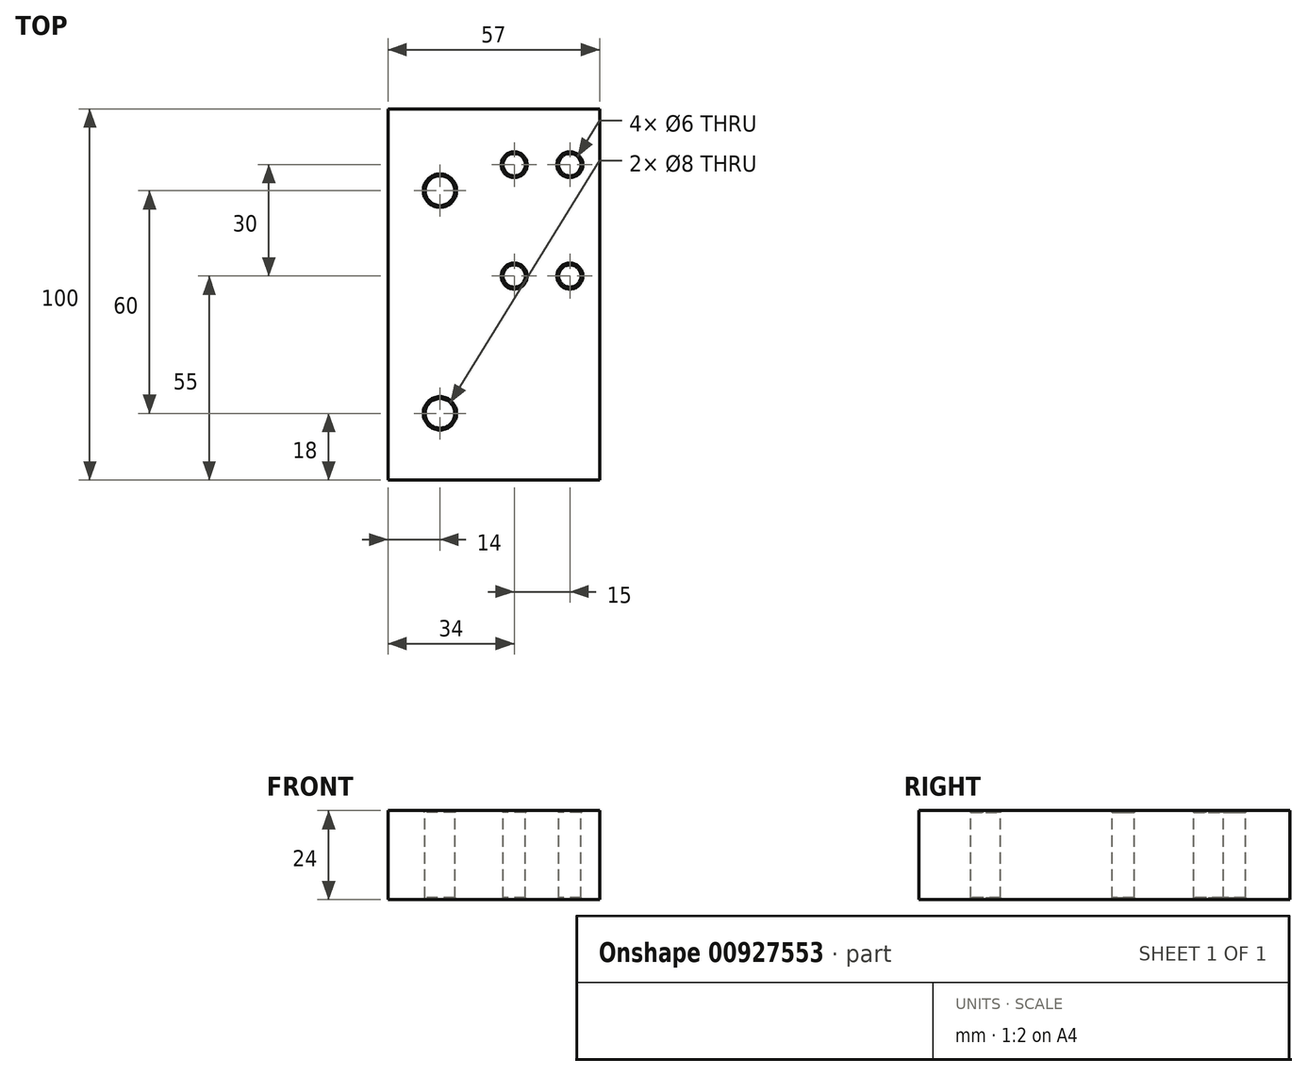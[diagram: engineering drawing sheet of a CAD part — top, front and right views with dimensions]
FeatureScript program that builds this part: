
annotation { "Feature Type Name" : "Feature", "Feature Type Description" : "" }
export const myFeature = defineFeature(function(context is Context, id is Id, definition is map)
    precondition{}
    {
        {
            var Q0;
            Q0=qCreatedBy(makeId("Right.planeOp"),FACE);
            var sketch = newSketch(context, id + "F0", { "sketchPlane" : qUnion([Q0])});
            skLineSegment(sketch, "E0.bottom", {"start": v(50, -12) * mm, "end": v(-50, -12) * mm});
            skLineSegment(sketch, "E0.top", {"start": v(50, 12) * mm, "end": v(-50, 12) * mm});
            skLineSegment(sketch, "E0.left", {"start": v(50, -12) * mm, "end": v(50, 12) * mm});
            skLineSegment(sketch, "E0.right", {"start": v(-50, -12) * mm, "end": v(-50, 12) * mm});
            skPoint(sketch, "E0.middle", {"position": v(0, 0) * mm});
            skSolve(sketch);
        }
        {
            var Q0;
            Q0 = qSketchRegion(id + "F0", true);
            extrude(context, id + "F1", {"entities" : qUnion([Q0]), "oppositeDirection" : true, "depth" : 22 * mm, "offsetDistance" : 25 * mm});
        }
        {
            var Q0;
            Q0=makeQuery(id+"F1.opExtrude","SWEPT_FACE",FACE,{"disambiguationData":[OSD([sQuery(id+"F0.wireOp",EDGE,"E0.top")])]});
            var sketch = newSketch(context, id + "F2", { "sketchPlane" : qUnion([Q0])});
            skLineSegment(sketch, "E1", {"start": v(-63.87, 28) * mm, "end": v(57.84, 28) * mm, "construction": true});
            skLineSegment(sketch, "E2", {"start": v(-8, 56.96) * mm, "end": v(-8, -60.17) * mm, "construction": true});
            skCircle(sketch, "E3", {"center": v(-8, 28) * mm, "radius": 4 * mm});
            skCircle(sketch, "E4", {"center": v(-8, -32) * mm, "radius": 4 * mm});
            skLineSegment(sketch, "E5", {"start": v(-58.28, -2) * mm, "end": v(56.2, -2) * mm, "construction": true});
            skSolve(sketch);
        }
        {
            var Q0;
            Q0 = qSketchRegion(id + "F2", true);
            extrude(context, id + "F3", {"entities" : qUnion([Q0]), "operationType" : NewBodyOperationType.REMOVE, "endBound" : BoundingType.THROUGH_ALL, "oppositeDirection" : true, "depth" : 25 * mm, "offsetDistance" : 25 * mm});
        }
        {
            var Q0;
            Q0=makeQuery(id+"F3.boolean.opBoolean","COPY",FACE,{"derivedFrom":makeQuery(id+"F3.opExtrude","SWEPT_FACE",FACE,{"disambiguationData":[OSD([sQuery(id+"F2.wireOp",EDGE,"E3")])]})});
            var Q1;
            Q1=makeQuery(id+"F3.boolean.opBoolean","COPY",FACE,{"derivedFrom":makeQuery(id+"F3.opExtrude","SWEPT_FACE",FACE,{"disambiguationData":[OSD([sQuery(id+"F2.wireOp",EDGE,"E4")])]})});
            chamfer(context, id + "F4", {"entities" : qUnion([Q0, Q1]), "width" : 0.5 * mm, "tangentPropagation" : true});
        }
        {
            var Q0;
            Q0=makeQuery(id+"F1.opExtrude","CAP_FACE",FACE,{"disambiguationData":[OSD([sQuery(id+"F0.wireOp",EDGE,"E0.bottom"),sQuery(id+"F0.wireOp",EDGE,"E0.top"),sQuery(id+"F0.wireOp",EDGE,"E0.left"),sQuery(id+"F0.wireOp",EDGE,"E0.right")])],"isStart":true});
            var sketch = newSketch(context, id + "F5", { "sketchPlane" : qUnion([Q0])});
            skLineSegment(sketch, "E6", {"start": v(35, 33.56) * mm, "end": v(35, -35.07) * mm, "construction": true});
            skLineSegment(sketch, "E7", {"start": v(5, 29.86) * mm, "end": v(5, -24.68) * mm, "construction": true});
            skLineSegment(sketch, "E8", {"start": v(50, 13.58) * mm, "end": v(50, -15.06) * mm, "construction": true});
            skLineSegment(sketch, "E9", {"start": v(-50, 13.27) * mm, "end": v(-50, -17.52) * mm, "construction": true});
            skLineSegment(sketch, "E10", {"start": v(-50, 12) * mm, "end": v(50, 12) * mm});
            skLineSegment(sketch, "E11", {"start": v(50, 12) * mm, "end": v(50, -12) * mm});
            skLineSegment(sketch, "E12", {"start": v(50, -12) * mm, "end": v(-50, -12) * mm});
            skLineSegment(sketch, "E13", {"start": v(-50, -12) * mm, "end": v(-50, 12) * mm});
            skSolve(sketch);
        }
        {
            var Q0;
            Q0 = qSketchRegion(id + "F5", true);
            extrude(context, id + "F6", {"entities" : qUnion([Q0]), "operationType" : NewBodyOperationType.ADD, "depth" : 35 * mm, "offsetDistance" : 25 * mm});
        }
        {
            var Q0;
            Q0=makeQuery(id+"F6.boolean.opBoolean","MERGE",FACE,{"derivedFrom":[makeQuery(id+"F1.opExtrude","SWEPT_FACE",FACE,{"disambiguationData":[OSD([sQuery(id+"F0.wireOp",EDGE,"E0.top")])]}),makeQuery(id+"F6.opExtrude","SWEPT_FACE",FACE,{"disambiguationData":[OSD([sQuery(id+"F5.wireOp",EDGE,"E10")])]})]});
            var sketch = newSketch(context, id + "F7", { "sketchPlane" : qUnion([Q0])});
            skPoint(sketch, "E14.startSnap0", {"position": v(35, 0) * mm});
            skPoint(sketch, "E15.startSnap0", {"position": v(6.5, 50) * mm});
            skCircle(sketch, "E16", {"center": v(27, 5) * mm, "radius": 3 * mm});
            skLineSegment(sketch, "E17", {"start": v(27, 59.98) * mm, "end": v(27, -62.62) * mm, "construction": true});
            skCircle(sketch, "E18", {"center": v(27, 35) * mm, "radius": 3 * mm});
            skLineSegment(sketch, "E19", {"start": v(12, 60.17) * mm, "end": v(12, -64.13) * mm, "construction": true});
            skCircle(sketch, "E20", {"center": v(12, 35) * mm, "radius": 3 * mm});
            skCircle(sketch, "E21", {"center": v(12, 5) * mm, "radius": 3 * mm});
            skSolve(sketch);
        }
        {
            var Q0;
            Q0 = qSketchRegion(id + "F7", true);
            extrude(context, id + "F8", {"entities" : qUnion([Q0]), "operationType" : NewBodyOperationType.REMOVE, "endBound" : BoundingType.THROUGH_ALL, "oppositeDirection" : true, "depth" : 25 * mm, "offsetDistance" : 25 * mm});
        }
        {
            var Q0;
            Q0=makeQuery(id+"F8.boolean.opBoolean","COPY",FACE,{"derivedFrom":makeQuery(id+"F8.opExtrude","SWEPT_FACE",FACE,{"disambiguationData":[OSD([sQuery(id+"F7.wireOp",EDGE,"E16")])]})});
            var Q1;
            Q1=makeQuery(id+"F8.boolean.opBoolean","COPY",FACE,{"derivedFrom":makeQuery(id+"F8.opExtrude","SWEPT_FACE",FACE,{"disambiguationData":[OSD([sQuery(id+"F7.wireOp",EDGE,"E18")])]})});
            var Q2;
            Q2=makeQuery(id+"F8.boolean.opBoolean","COPY",FACE,{"derivedFrom":makeQuery(id+"F8.opExtrude","SWEPT_FACE",FACE,{"disambiguationData":[OSD([sQuery(id+"F7.wireOp",EDGE,"E20")])]})});
            var Q3;
            Q3=makeQuery(id+"F8.boolean.opBoolean","COPY",FACE,{"derivedFrom":makeQuery(id+"F8.opExtrude","SWEPT_FACE",FACE,{"disambiguationData":[OSD([sQuery(id+"F7.wireOp",EDGE,"E21")])]})});
            chamfer(context, id + "F9", {"entities" : qUnion([Q0, Q1, Q2, Q3]), "width" : 0.5 * mm, "tangentPropagation" : true});
        }
    });
